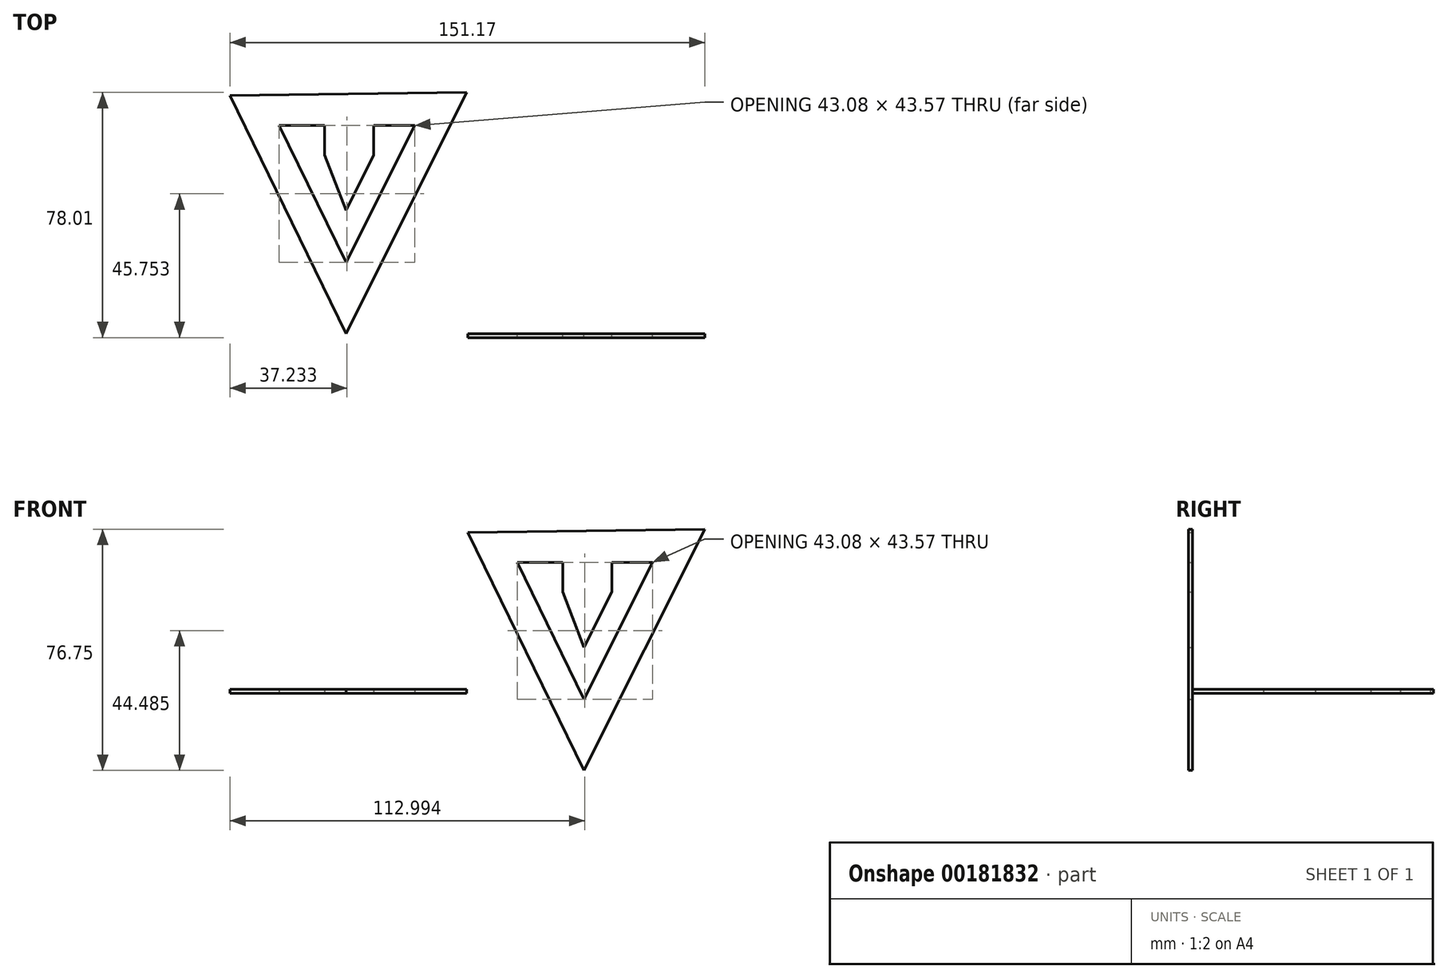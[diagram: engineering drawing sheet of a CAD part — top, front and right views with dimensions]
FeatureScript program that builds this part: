
annotation { "Feature Type Name" : "Feature", "Feature Type Description" : "" }
export const myFeature = defineFeature(function(context is Context, id is Id, definition is map)
    precondition{}
    {
        {
            var Q0;
            Q0=qCreatedBy(makeId("Top.planeOp"),FACE);
            var sketch = newSketch(context, id + "F0", { "sketchPlane" : qUnion([Q0])});
            skLineSegment(sketch, "E0", {"start": v(-75.4, 75.76) * mm, "end": v(-38.48, 0) * mm});
            skLineSegment(sketch, "E1", {"start": v(-38.48, 0) * mm, "end": v(0, 76.74) * mm});
            skLineSegment(sketch, "E2", {"start": v(0, 76.74) * mm, "end": v(-75.4, 75.76) * mm});
            skLineSegment(sketch, "E3", {"start": v(-59.72, 66.27) * mm, "end": v(-38.48, 22.7) * mm});
            skLineSegment(sketch, "E4", {"start": v(-38.48, 22.7) * mm, "end": v(-16.64, 66.27) * mm});
            skLineSegment(sketch, "E5", {"start": v(-16.64, 66.27) * mm, "end": v(-29.62, 66.27) * mm});
            skLineSegment(sketch, "E6", {"start": v(-45.22, 56.83) * mm, "end": v(-38.48, 39.15) * mm});
            skLineSegment(sketch, "E7", {"start": v(-38.48, 39.15) * mm, "end": v(-29.62, 56.83) * mm});
            skLineSegment(sketch, "E8", {"start": v(-45.22, 56.83) * mm, "end": v(-45.22, 66.27) * mm});
            skLineSegment(sketch, "E9", {"start": v(-29.62, 66.27) * mm, "end": v(-29.62, 66.27) * mm});
            skLineSegment(sketch, "E10", {"start": v(-45.22, 66.27) * mm, "end": v(-45.22, 66.27) * mm});
            skLineSegment(sketch, "E11", {"start": v(-29.62, 66.27) * mm, "end": v(-29.62, 56.83) * mm});
            skLineSegment(sketch, "E12", {"start": v(-44.67, 66.27) * mm, "end": v(-45.22, 66.27) * mm});
            skLineSegment(sketch, "E13", {"start": v(-45.22, 66.27) * mm, "end": v(-59.72, 66.27) * mm});
            skSolve(sketch);
        }
        {
            var Q0;
            Q0=makeQuery(id+"F0.imprint","IMPRINT",FACE,{"disambiguationData":[TD([[makeQuery(id+"F0.imprint","IMPRINT",EDGE,{"derivedFrom":sQuery(id+"F0.wireOp",EDGE,"E6")}),1.0]])]});
            var Q1;
            Q1=makeQuery(id+"F0.imprint","IMPRINT",FACE,{"disambiguationData":[TD([[makeQuery(id+"F0.imprint","IMPRINT",EDGE,{"derivedFrom":sQuery(id+"F0.wireOp",EDGE,"E0")}),1.0]])]});
            extrude(context, id + "F1", {"entities" : qUnion([Q0, Q1]), "depth" : 1.27 * mm});
        }
        {
            var Q0;
            Q0=qCreatedBy(makeId("Front.planeOp"),FACE);
            var sketch = newSketch(context, id + "F2", { "sketchPlane" : qUnion([Q0])});
            skLineSegment(sketch, "E14", {"start": v(0.35, 51.22) * mm, "end": v(37.28, -24.54) * mm});
            skLineSegment(sketch, "E15", {"start": v(37.28, -24.54) * mm, "end": v(75.76, 52.2) * mm});
            skLineSegment(sketch, "E16", {"start": v(75.76, 52.2) * mm, "end": v(0.35, 51.22) * mm});
            skLineSegment(sketch, "E17", {"start": v(16.04, 41.73) * mm, "end": v(37.28, -1.84) * mm});
            skLineSegment(sketch, "E18", {"start": v(37.28, -1.84) * mm, "end": v(59.12, 41.73) * mm});
            skLineSegment(sketch, "E19", {"start": v(59.12, 41.73) * mm, "end": v(46.14, 41.73) * mm});
            skLineSegment(sketch, "E20", {"start": v(30.54, 32.29) * mm, "end": v(37.28, 14.6) * mm});
            skLineSegment(sketch, "E21", {"start": v(37.28, 14.6) * mm, "end": v(46.14, 32.29) * mm});
            skLineSegment(sketch, "E22", {"start": v(30.54, 32.29) * mm, "end": v(30.54, 41.73) * mm});
            skLineSegment(sketch, "E23", {"start": v(46.14, 41.73) * mm, "end": v(46.14, 41.73) * mm});
            skLineSegment(sketch, "E24", {"start": v(30.54, 41.73) * mm, "end": v(30.54, 41.73) * mm});
            skLineSegment(sketch, "E25", {"start": v(46.14, 41.73) * mm, "end": v(46.14, 32.29) * mm});
            skLineSegment(sketch, "E26", {"start": v(31.1, 41.73) * mm, "end": v(30.54, 41.73) * mm});
            skLineSegment(sketch, "E27", {"start": v(30.54, 41.73) * mm, "end": v(16.04, 41.73) * mm});
            skSolve(sketch);
        }
        {
            var Q0;
            Q0=makeQuery(id+"F2.imprint","IMPRINT",FACE,{"disambiguationData":[TD([[makeQuery(id+"F2.imprint","IMPRINT",EDGE,{"derivedFrom":sQuery(id+"F2.wireOp",EDGE,"E14")}),1.0]])]});
            extrude(context, id + "F3", {"entities" : qUnion([Q0]), "depth" : 1.27 * mm});
        }
    });
